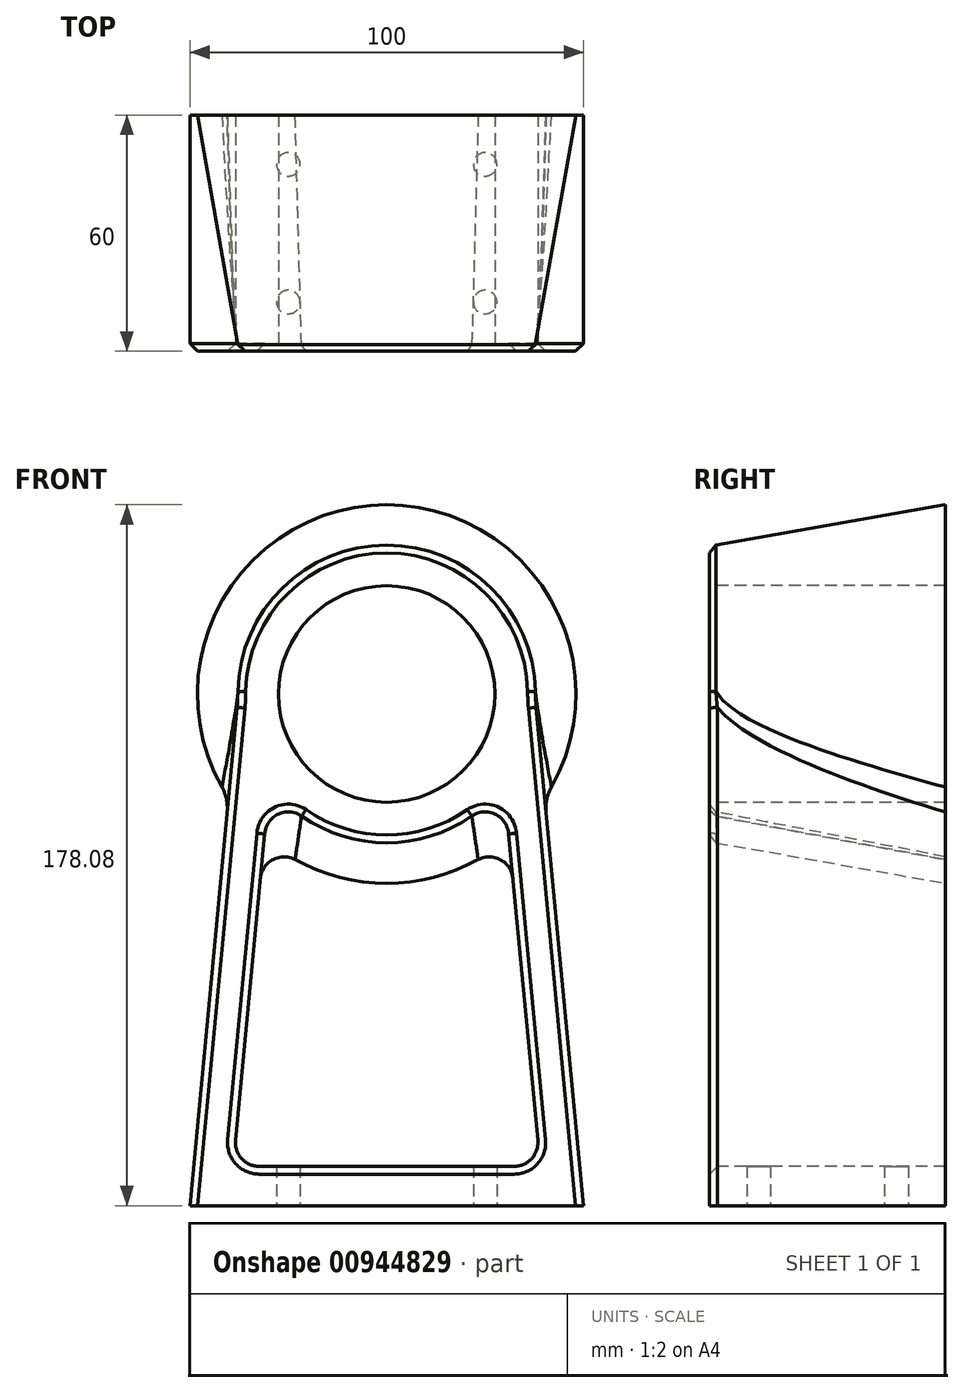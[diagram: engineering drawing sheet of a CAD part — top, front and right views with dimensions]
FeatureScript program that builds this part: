
annotation { "Feature Type Name" : "Feature", "Feature Type Description" : "" }
export const myFeature = defineFeature(function(context is Context, id is Id, definition is map)
    precondition{}
    {
        {
            var Q0;
            Q0=qCreatedBy(makeId("Front.planeOp"),FACE);
            var sketch = newSketch(context, id + "F0", { "sketchPlane" : qUnion([Q0])});
            skLineSegment(sketch, "E0.top", {"start": v(-50, -99.3) * mm, "end": v(50, -99.3) * mm});
            skLineSegment(sketch, "E1", {"start": v(0, 121.96) * mm, "end": v(0, -115.93) * mm, "construction": true});
            skCircle(sketch, "E2", {"center": v(0, 30.7) * mm, "radius": 27.5 * mm});
            skLineSegment(sketch, "E3", {"start": v(-38.38, -82.73) * mm, "end": v(-29.78, 7.92) * mm});
            skLineSegment(sketch, "E4", {"start": v(38.38, -82.73) * mm, "end": v(29.78, 7.92) * mm});
            skLineSegment(sketch, "E5.0", {"start": v(-50, -99.3) * mm, "end": v(-37.33, 34.24) * mm});
            skLineSegment(sketch, "E6.0", {"start": v(50, -99.3) * mm, "end": v(37.33, 34.24) * mm});
            skArc(sketch, "E7", {"start": v(-29.78, 7.92) * mm, "mid": v(0, -6.8) * mm, "end": v(29.78, 7.92) * mm});
            skArc(sketch, "E8.trimOffspring", {"start": v(37.33, 34.24) * mm, "mid": v(0, 68.2) * mm, "end": v(-37.33, 34.24) * mm});
            skLineSegment(sketch, "E9.trimOffspring", {"start": v(-32.41, -89.3) * mm, "end": v(32.41, -89.3) * mm});
            skPoint(sketch, "E10.visualSharp", {"position": v(-29.78, 7.92) * mm});
            skPoint(sketch, "E11.visualSharp", {"position": v(29.78, 7.92) * mm});
            skPoint(sketch, "E12.visualSharp", {"position": v(-39, -89.3) * mm});
            skArc(sketch, "E12.filletArc", {"start": v(-38.38, -82.73) * mm, "mid": v(-36.85, -87.34) * mm, "end": v(-32.41, -89.3) * mm});
            skPoint(sketch, "E13.visualSharp", {"position": v(39, -89.3) * mm});
            skArc(sketch, "E13.filletArc", {"start": v(32.41, -89.3) * mm, "mid": v(36.85, -87.34) * mm, "end": v(38.38, -82.73) * mm});
            skPoint(sketch, "E14.orphan", {"position": v(-49.96, -99.3) * mm});
            skPoint(sketch, "E15.orphan", {"position": v(50.15, -99.3) * mm});
            skSolve(sketch);
        }
        {
            var Q0;
            Q0 = qSketchRegion(id + "F0", true);
            extrude(context, id + "F1", {"entities" : qUnion([Q0]), "oppositeDirection" : true, "depth" : 60 * mm, "offsetDistance" : 25 * mm});
        }
        {
            var Q0;
            Q0=makeQuery(id+"F1.opExtrude","CAP_FACE",FACE,{"disambiguationData":[OSD([sQuery(id+"F0.wireOp",EDGE,"E0.top"),sQuery(id+"F0.wireOp",EDGE,"E2"),sQuery(id+"F0.wireOp",EDGE,"E3"),sQuery(id+"F0.wireOp",EDGE,"E4"),sQuery(id+"F0.wireOp",EDGE,"E5.0"),sQuery(id+"F0.wireOp",EDGE,"E6.0"),sQuery(id+"F0.wireOp",EDGE,"E7"),sQuery(id+"F0.wireOp",EDGE,"E8.trimOffspring"),sQuery(id+"F0.wireOp",EDGE,"E9.trimOffspring"),sQuery(id+"F0.wireOp",EDGE,"E10.filletArc"),sQuery(id+"F0.wireOp",EDGE,"E11.filletArc"),sQuery(id+"F0.wireOp",EDGE,"E12.filletArc"),sQuery(id+"F0.wireOp",EDGE,"E13.filletArc")])],"isStart":true});
            var sketch = newSketch(context, id + "F2", { "sketchPlane" : qUnion([Q0])});
            skCircle(sketch, "E16", {"center": v(0, 30.7) * mm, "radius": 37.5 * mm});
            skSolve(sketch);
        }
        {
            var Q0;
            Q0 = qSketchRegion(id + "F2", true);
            extrude(context, id + "F3", {"entities" : qUnion([Q0]), "operationType" : NewBodyOperationType.ADD, "oppositeDirection" : true, "depth" : 60 * mm, "offsetDistance" : 25 * mm, "hasDraft" : true, "draftAngle" : 10 * degree});
        }
        {
            var Q0;
            Q0=makeQuery(id+"F3.boolean.opBoolean","MERGE",FACE,{"derivedFrom":[makeQuery(id+"F1.opExtrude","CAP_FACE",FACE,{"disambiguationData":[OSD([sQuery(id+"F0.wireOp",EDGE,"E0.top"),sQuery(id+"F0.wireOp",EDGE,"E2"),sQuery(id+"F0.wireOp",EDGE,"E3"),sQuery(id+"F0.wireOp",EDGE,"E4"),sQuery(id+"F0.wireOp",EDGE,"E5.0"),sQuery(id+"F0.wireOp",EDGE,"E6.0"),sQuery(id+"F0.wireOp",EDGE,"E7"),sQuery(id+"F0.wireOp",EDGE,"E8.trimOffspring"),sQuery(id+"F0.wireOp",EDGE,"E9.trimOffspring"),sQuery(id+"F0.wireOp",EDGE,"E10.filletArc"),sQuery(id+"F0.wireOp",EDGE,"E11.filletArc"),sQuery(id+"F0.wireOp",EDGE,"E12.filletArc"),sQuery(id+"F0.wireOp",EDGE,"E13.filletArc")])],"isStart":true}),makeQuery(id+"F3.opExtrude","CAP_FACE",FACE,{"disambiguationData":[OSD([sQuery(id+"F2.wireOp",EDGE,"E16")])],"isStart":true})]});
            var sketch = newSketch(context, id + "F4", { "sketchPlane" : qUnion([Q0])});
            skCircle(sketch, "E17", {"center": v(0, 30.7) * mm, "radius": 27.5 * mm});
            skSolve(sketch);
        }
        {
            var Q0;
            Q0 = qSketchRegion(id + "F4", true);
            extrude(context, id + "F5", {"entities" : qUnion([Q0]), "operationType" : NewBodyOperationType.REMOVE, "endBound" : BoundingType.THROUGH_ALL, "oppositeDirection" : true, "depth" : 25 * mm, "offsetDistance" : 25 * mm});
        }
        {
            var Q0;
            Q0=makeQuery(id+"F3.boolean.opBoolean","INTERSECT",EDGE,{"derivedFrom":[makeQuery(id+"F1.opExtrude","SWEPT_FACE",FACE,{"disambiguationData":[OSD([sQuery(id+"F0.wireOp",EDGE,"E5.0")])]}),makeQuery(id+"F3.opExtrude","SWEPT_FACE",FACE,{"disambiguationData":[OSD([sQuery(id+"F2.wireOp",EDGE,"E16")])]})]});
            var Q1;
            Q1=makeQuery(id+"F3.boolean.opBoolean","INTERSECT",EDGE,{"derivedFrom":[makeQuery(id+"F1.opExtrude","SWEPT_FACE",FACE,{"disambiguationData":[OSD([sQuery(id+"F0.wireOp",EDGE,"E6.0")])]}),makeQuery(id+"F3.opExtrude","SWEPT_FACE",FACE,{"disambiguationData":[OSD([sQuery(id+"F2.wireOp",EDGE,"E16")])]})]});
            fillet(context, id + "F6", {"entities" : qUnion([Q0, Q1]), "radius" : 10 * mm, "tangentPropagation" : true, "allowEdgeOverflow" : false});
        }
        {
            var Q0;
            Q0=makeQuery(id+"F3.boolean.opBoolean","INTERSECT",EDGE,{"derivedFrom":[makeQuery(id+"F1.opExtrude","SWEPT_FACE",FACE,{"disambiguationData":[OSD([sQuery(id+"F0.wireOp",EDGE,"E3")])]}),makeQuery(id+"F3.opExtrude","SWEPT_FACE",FACE,{"disambiguationData":[OSD([sQuery(id+"F2.wireOp",EDGE,"E16")])]})]});
            var Q1;
            Q1=makeQuery(id+"F3.boolean.opBoolean","INTERSECT",EDGE,{"derivedFrom":[makeQuery(id+"F1.opExtrude","SWEPT_FACE",FACE,{"disambiguationData":[OSD([sQuery(id+"F0.wireOp",EDGE,"E4")])]}),makeQuery(id+"F3.opExtrude","SWEPT_FACE",FACE,{"disambiguationData":[OSD([sQuery(id+"F2.wireOp",EDGE,"E16")])]})]});
            fillet(context, id + "F7", {"entities" : qUnion([Q0, Q1]), "radius" : 6 * mm, "tangentPropagation" : true, "allowEdgeOverflow" : false});
        }
        {
            var Q0;
            Q0=makeQuery(id+"F1.opExtrude","CAP_EDGE",EDGE,{"disambiguationData":[OSD([sQuery(id+"F0.wireOp",EDGE,"E5.0")])],"isStart":true});
            var Q1;
            Q1=makeQuery(id+"F1.opExtrude","CAP_EDGE",EDGE,{"disambiguationData":[OSD([sQuery(id+"F0.wireOp",EDGE,"E3")])],"isStart":true});
            chamfer(context, id + "F8", {"entities" : qUnion([Q0, Q1]), "width" : 2 * mm, "tangentPropagation" : true});
        }
        {
            var Q0;
            Q0=makeQuery(id+"F1.opExtrude","SWEPT_FACE",FACE,{"disambiguationData":[OSD([sQuery(id+"F0.wireOp",EDGE,"E0.top")])]});
            var sketch = newSketch(context, id + "F9", { "sketchPlane" : qUnion([Q0])});
            skPoint(sketch, "E18", {"position": v(-25, -12.5) * mm});
            skPoint(sketch, "E19.0.1.0", {"position": v(-25, -47.5) * mm});
            skPoint(sketch, "E19.1.0.0", {"position": v(25, -12.5) * mm});
            skPoint(sketch, "E19.1.1.0", {"position": v(25, -47.5) * mm});
            skLineSegment(sketch, "E19.direction1", {"start": v(-25, -12.5) * mm, "end": v(25, -12.5) * mm, "construction": true});
            skLineSegment(sketch, "E19.direction2", {"start": v(-25, -12.5) * mm, "end": v(-25, -47.5) * mm, "construction": true});
            skSolve(sketch);
        }
        {
            var Q0;
            Q0=sQuery(id+"F9.wireOp",VERTEX,"E18");
            var Q1;
            Q1=sQuery(id+"F9.wireOp",VERTEX,"E19.0.1.0");
            var Q2;
            Q2=sQuery(id+"F9.wireOp",VERTEX,"E19.1.0.0");
            var Q3;
            Q3=sQuery(id+"F9.wireOp",VERTEX,"E19.1.1.0");
            var Q4;
            Q4=makeQuery(id+"F1.opExtrude","SWEPT_BODY",BODY,{"disambiguationData":[OSD([sQuery(id+"F0.wireOp",EDGE,"E0.top"),sQuery(id+"F0.wireOp",EDGE,"E2"),sQuery(id+"F0.wireOp",EDGE,"E3"),sQuery(id+"F0.wireOp",EDGE,"E4"),sQuery(id+"F0.wireOp",EDGE,"E5.0"),sQuery(id+"F0.wireOp",EDGE,"E6.0"),sQuery(id+"F0.wireOp",EDGE,"E7"),sQuery(id+"F0.wireOp",EDGE,"E8.trimOffspring"),sQuery(id+"F0.wireOp",EDGE,"E9.trimOffspring"),sQuery(id+"F0.wireOp",EDGE,"E12.filletArc"),sQuery(id+"F0.wireOp",EDGE,"E13.filletArc")])]});
            hole(context, id + "F10", {"style" : HoleStyle.SIMPLE, "endStyle" : HoleEndStyle.BLIND, "holeDiameter" : 6 * mm, "majorDiameter" : 5 * mm, "holeDepth" : 12 * mm, "isTappedThrough" : true, "tappedDepth" : 20.5 * mm, "tapClearance" : 3, "locations" : qUnion([Q0, Q1, Q2, Q3]), "scope" : qUnion([Q4])});
        }
    });
